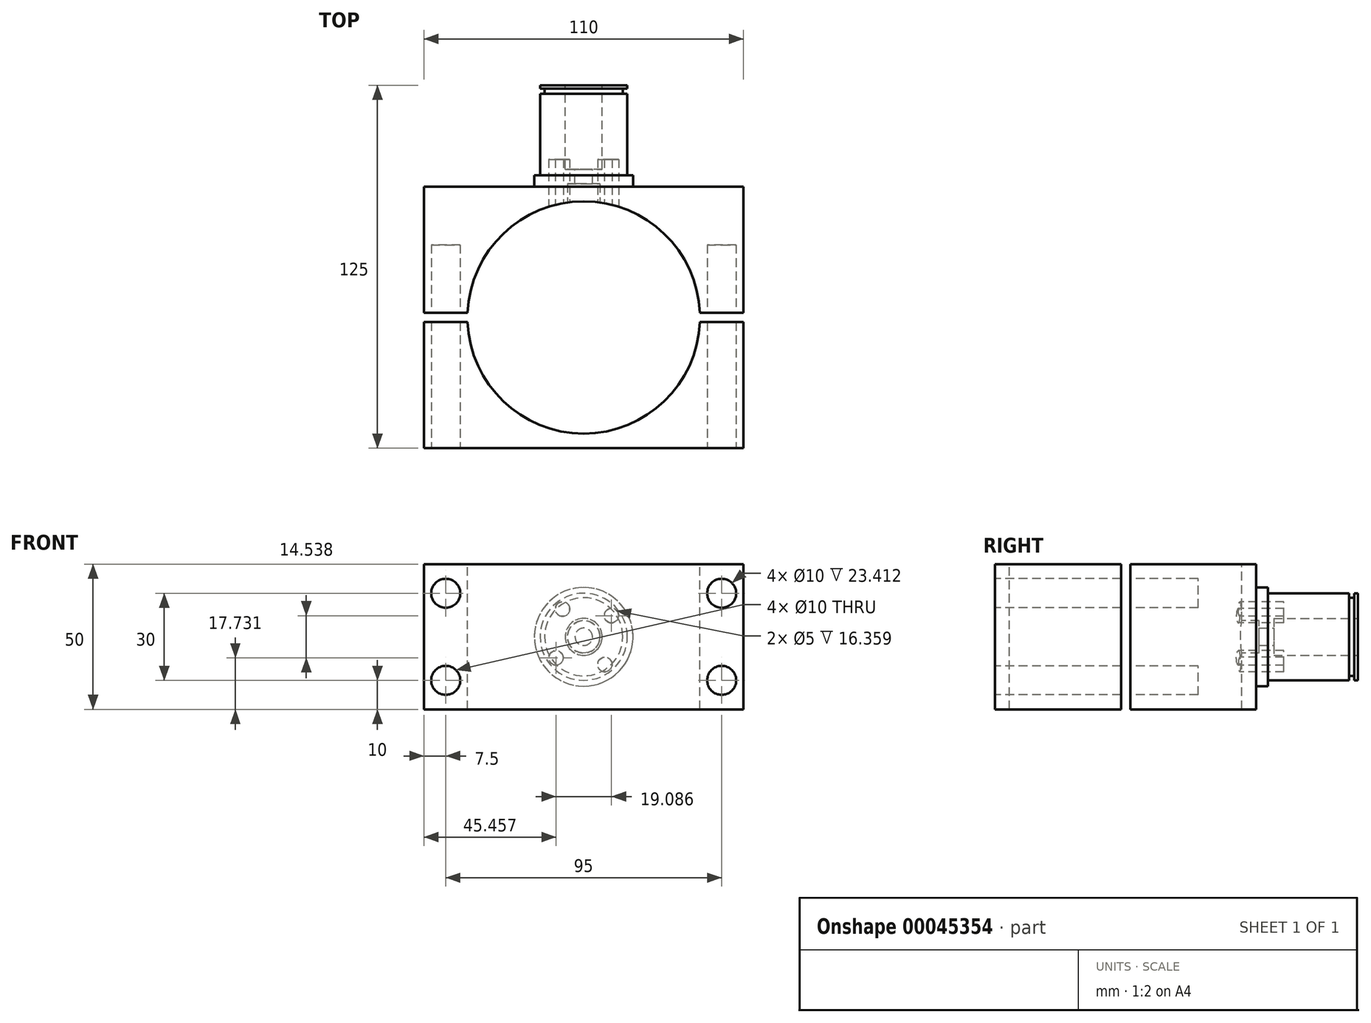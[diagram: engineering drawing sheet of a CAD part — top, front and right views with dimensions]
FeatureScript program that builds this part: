
annotation { "Feature Type Name" : "Feature", "Feature Type Description" : "" }
export const myFeature = defineFeature(function(context is Context, id is Id, definition is map)
    precondition{}
    {
        {
            var Q0;
            Q0=qCreatedBy(makeId("Front.planeOp"),FACE);
            var sketch = newSketch(context, id + "F0", { "sketchPlane" : qUnion([Q0])});
            skCircle(sketch, "E0", {"center": v(0, 0) * mm, "radius": 15 * mm});
            skCircle(sketch, "E1", {"center": v(0, 0) * mm, "radius": 6.36 * mm});
            skSolve(sketch);
        }
        {
            var Q0;
            Q0 = qSketchRegion(id + "F0", true);
            extrude(context, id + "F1", {"entities" : qUnion([Q0]), "depth" : 35 * mm});
        }
        {
            var Q0;
            Q0=makeQuery(id+"F1.opExtrude","CAP_FACE",FACE,{"disambiguationData":[OSD([sQuery(id+"F0.wireOp",EDGE,"E0"),sQuery(id+"F0.wireOp",EDGE,"E1")])],"isStart":false});
            var sketch = newSketch(context, id + "F2", { "sketchPlane" : qUnion([Q0])});
            skLineSegment(sketch, "E2.bottom", {"start": v(-55, 25) * mm, "end": v(55, 25) * mm});
            skLineSegment(sketch, "E2.top", {"start": v(-55, -25) * mm, "end": v(55, -25) * mm});
            skLineSegment(sketch, "E2.left", {"start": v(-55, 25) * mm, "end": v(-55, -25) * mm});
            skLineSegment(sketch, "E2.right", {"start": v(55, 25) * mm, "end": v(55, -25) * mm});
            skSolve(sketch);
        }
        {
            var Q0;
            Q0 = qSketchRegion(id + "F2", true);
            extrude(context, id + "F3", {"entities" : qUnion([Q0]), "operationType" : NewBodyOperationType.ADD, "depth" : 90 * mm});
        }
        {
            var Q0;
            Q0=makeQuery(id+"F3.opExtrude","CAP_FACE",FACE,{"disambiguationData":[OSD([sQuery(id+"F2.wireOp",EDGE,"E2.bottom"),sQuery(id+"F2.wireOp",EDGE,"E2.top"),sQuery(id+"F2.wireOp",EDGE,"E2.left"),sQuery(id+"F2.wireOp",EDGE,"E2.right")])],"isStart":false});
            var sketch = newSketch(context, id + "F4", { "sketchPlane" : qUnion([Q0])});
            skCircle(sketch, "E3", {"center": v(-47.5, 15) * mm, "radius": 5 * mm});
            skCircle(sketch, "E4.0.1.0", {"center": v(-47.5, -15) * mm, "radius": 5 * mm});
            skCircle(sketch, "E4.1.0.0", {"center": v(47.5, 15) * mm, "radius": 5 * mm});
            skCircle(sketch, "E4.1.1.0", {"center": v(47.5, -15) * mm, "radius": 5 * mm});
            skLineSegment(sketch, "E4.direction1", {"start": v(-47.5, 15) * mm, "end": v(47.5, 15) * mm, "construction": true});
            skLineSegment(sketch, "E4.direction2", {"start": v(-47.5, 15) * mm, "end": v(-47.5, -15) * mm, "construction": true});
            skSolve(sketch);
        }
        {
            var Q0;
            Q0 = qSketchRegion(id + "F4", true);
            var Q1;
            Q1=makeQuery(id+"F7.boolean.opBoolean","COPY",FACE,{"derivedFrom":makeQuery(id+"F7.opExtrude","SWEPT_FACE",FACE,{"disambiguationData":[OSD([sQuery(id+"F6.wireOp",EDGE,"E6.bottom")])]})});
            var Q2;
            Q2=makeQuery(id+"F7.boolean.opBoolean","COPY",FACE,{"derivedFrom":makeQuery(id+"F7.opExtrude","SWEPT_FACE",FACE,{"disambiguationData":[OSD([sQuery(id+"F6.wireOp",EDGE,"E7.trimOffspring")])]})});
            extrude(context, id + "F5", {"entities" : qUnion([Q0, Q1, Q2]), "operationType" : NewBodyOperationType.REMOVE, "oppositeDirection" : true, "depth" : 70 * mm});
        }
        {
            var Q0;
            Q0=makeQuery(id+"F3.opExtrude","SWEPT_FACE",FACE,{"disambiguationData":[OSD([sQuery(id+"F2.wireOp",EDGE,"E2.bottom")])]});
            var sketch = newSketch(context, id + "F6", { "sketchPlane" : qUnion([Q0])});
            skArc(sketch, "E5", {"start": v(-39.97, -81.59) * mm, "mid": v(0, -120) * mm, "end": v(39.97, -81.59) * mm});
            skLineSegment(sketch, "E6.bottom", {"start": v(-59, -78.41) * mm, "end": v(-39.97, -78.41) * mm});
            skLineSegment(sketch, "E6.top", {"start": v(-59, -81.59) * mm, "end": v(-39.97, -81.59) * mm});
            skLineSegment(sketch, "E6.left", {"start": v(-59, -78.41) * mm, "end": v(-59, -81.59) * mm});
            skLineSegment(sketch, "E6.right", {"start": v(59.74, -78.41) * mm, "end": v(59.74, -81.59) * mm});
            skLineSegment(sketch, "E7.trimOffspring", {"start": v(39.97, -78.41) * mm, "end": v(59.74, -78.41) * mm});
            skLineSegment(sketch, "E8.trimOffspring", {"start": v(39.97, -81.59) * mm, "end": v(59.74, -81.59) * mm});
            skArc(sketch, "E9.trimOffspring", {"start": v(39.97, -78.41) * mm, "mid": v(0, -40) * mm, "end": v(-39.97, -78.41) * mm});
            skSolve(sketch);
        }
        {
            var Q0;
            Q0 = qSketchRegion(id + "F6", true);
            extrude(context, id + "F7", {"entities" : qUnion([Q0]), "operationType" : NewBodyOperationType.REMOVE, "endBound" : BoundingType.THROUGH_ALL, "oppositeDirection" : true, "depth" : 25 * mm});
        }
        {
            var Q0;
            Q0=makeQuery(id+"F1.opExtrude","CAP_FACE",FACE,{"disambiguationData":[OSD([sQuery(id+"F0.wireOp",EDGE,"E0"),sQuery(id+"F0.wireOp",EDGE,"E1")])],"isStart":true});
            var sketch = newSketch(context, id + "F8", { "sketchPlane" : qUnion([Q0])});
            skCircle(sketch, "E10", {"center": v(0, 0) * mm, "radius": 13.45 * mm});
            skCircle(sketch, "E11", {"center": v(0, 0) * mm, "radius": 15 * mm});
            skSolve(sketch);
        }
        {
            var Q0;
            Q0 = qSketchRegion(id + "F8", true);
            extrude(context, id + "F9", {"entities" : qUnion([Q0]), "operationType" : NewBodyOperationType.REMOVE, "oppositeDirection" : true, "depth" : 3 * mm});
        }
        {
            var Q0;
            Q0=makeQuery(id+"F1.opExtrude","CAP_FACE",FACE,{"disambiguationData":[OSD([sQuery(id+"F0.wireOp",EDGE,"E0"),sQuery(id+"F0.wireOp",EDGE,"E1")])],"isStart":true});
            var sketch = newSketch(context, id + "F10", { "sketchPlane" : qUnion([Q0])});
            skCircle(sketch, "E12", {"center": v(0, 0) * mm, "radius": 15 * mm});
            skCircle(sketch, "E13", {"center": v(0, 0) * mm, "radius": 13.45 * mm});
            skSolve(sketch);
        }
        {
            var Q0;
            Q0 = qSketchRegion(id + "F10", true);
            extrude(context, id + "F11", {"entities" : qUnion([Q0]), "operationType" : NewBodyOperationType.ADD, "oppositeDirection" : true, "depth" : 1.22 * mm});
        }
        {
            var Q0;
            {var subQ0=sQuery(id+"F2.wireOp",EDGE,"E2.left");var subQ1=sQuery(id+"F2.wireOp",EDGE,"E2.bottom");var subQ2=sQuery(id+"F2.wireOp",EDGE,"E2.top");var subQ3=sQuery(id+"F2.wireOp",EDGE,"E2.right");Q0=makeQuery(id+"F3.boolean.opBoolean","SPLIT",FACE,{"disambiguationData":[TD([makeQuery(id+"F1.opExtrude","SWEPT_FACE",FACE,{"disambiguationData":[OSD([sQuery(id+"F0.wireOp",EDGE,"E0")])]})])],"derivedFrom":makeQuery(id+"F3.opExtrude","CAP_FACE",FACE,{"disambiguationData":[OSD([subQ1,subQ2,subQ0,subQ3])],"isStart":true})});}
            var sketch = newSketch(context, id + "F12", { "sketchPlane" : qUnion([Q0])});
            skCircle(sketch, "E14", {"center": v(0, 0) * mm, "radius": 17 * mm});
            skSolve(sketch);
        }
        {
            var Q0;
            Q0=makeQuery(id+"F12.imprint","IMPRINT",FACE,{"disambiguationData":[TD([[makeQuery(id+"F12.imprint","IMPRINT",EDGE,{"derivedFrom":sQuery(id+"F12.wireOp",EDGE,"E14")}),1.0]])]});
            extrude(context, id + "F13", {"entities" : qUnion([Q0]), "operationType" : NewBodyOperationType.ADD, "depth" : 4 * mm});
        }
        {
            var Q0;
            Q0=makeQuery(id+"F3.boolean.opBoolean","SPLIT",FACE,{"disambiguationData":[TD([makeQuery(id+"F1.opExtrude","SWEPT_FACE",FACE,{"disambiguationData":[OSD([sQuery(id+"F0.wireOp",EDGE,"E1")])]})])],"derivedFrom":makeQuery(id+"F3.opExtrude","CAP_FACE",FACE,{"disambiguationData":[OSD([sQuery(id+"F2.wireOp",EDGE,"E2.bottom"),sQuery(id+"F2.wireOp",EDGE,"E2.top"),sQuery(id+"F2.wireOp",EDGE,"E2.left"),sQuery(id+"F2.wireOp",EDGE,"E2.right")])],"isStart":true})});
            var sketch = newSketch(context, id + "F14", { "sketchPlane" : qUnion([Q0])});
            skCircle(sketch, "E15", {"center": v(0, 0) * mm, "radius": 7.83 * mm});
            skSolve(sketch);
        }
        {
            var Q0;
            Q0 = qSketchRegion(id + "F14", true);
            extrude(context, id + "F15", {"entities" : qUnion([Q0]), "operationType" : NewBodyOperationType.ADD, "depth" : 6 * mm});
        }
        {
            var Q0;
            Q0=makeQuery(id+"F15.opExtrude","CAP_FACE",FACE,{"disambiguationData":[OSD([sQuery(id+"F14.wireOp",EDGE,"E15")])],"isStart":false});
            var sketch = newSketch(context, id + "F16", { "sketchPlane" : qUnion([Q0])});
            skCircle(sketch, "E16", {"center": v(0, 0) * mm, "radius": 3 * mm});
            skSolve(sketch);
        }
        {
            var Q0;
            Q0 = qSketchRegion(id + "F16", true);
            extrude(context, id + "F17", {"entities" : qUnion([Q0]), "operationType" : NewBodyOperationType.REMOVE, "oppositeDirection" : true, "depth" : 25 * mm});
        }
        {
            var Q0;
            Q0=qCreatedBy(makeId("Front.planeOp"),FACE);
            cPlane(context, id + "F18", {"entities" : qUnion([Q0]), "cplaneType" : CPlaneType.OFFSET, "offset" : 40.5 * mm, "width" : 150 * mm, "height" : 150 * mm});
        }
        {
            var Q0;
            Q0=qCreatedBy(id+"F18.planeOp",FACE);
            var sketch = newSketch(context, id + "F19", { "sketchPlane" : qUnion([Q0])});
            skCircle(sketch, "E17", {"center": v(0, 0) * mm, "radius": 5.6 * mm});
            skCircle(sketch, "E18", {"center": v(-7.27, 9.54) * mm, "radius": 2.5 * mm});
            skCircle(sketch, "E19.1.0", {"center": v(-9.54, -7.27) * mm, "radius": 2.5 * mm});
            skCircle(sketch, "E19.2.0", {"center": v(7.27, -9.54) * mm, "radius": 2.5 * mm});
            skCircle(sketch, "E19.3.0", {"center": v(9.54, 7.27) * mm, "radius": 2.5 * mm});
            skSolve(sketch);
        }
        {
            var Q0;
            Q0=makeQuery(id+"F19.imprint","IMPRINT",FACE,{"disambiguationData":[TD([[makeQuery(id+"F19.imprint","IMPRINT",EDGE,{"derivedFrom":sQuery(id+"F19.wireOp",EDGE,"E17")}),1.0]])]});
            extrude(context, id + "F20", {"entities" : qUnion([Q0]), "operationType" : NewBodyOperationType.REMOVE, "oppositeDirection" : true, "depth" : 6.5 * mm});
        }
        {
            var Q0;
            Q0=makeQuery(id+"F19.imprint","IMPRINT",FACE,{"disambiguationData":[TD([[makeQuery(id+"F19.imprint","IMPRINT",EDGE,{"derivedFrom":sQuery(id+"F19.wireOp",EDGE,"E19.2.0")}),1.0]])]});
            var Q1;
            Q1=makeQuery(id+"F19.imprint","IMPRINT",FACE,{"disambiguationData":[TD([[makeQuery(id+"F19.imprint","IMPRINT",EDGE,{"derivedFrom":sQuery(id+"F19.wireOp",EDGE,"E19.3.0")}),1.0]])]});
            var Q2;
            Q2=makeQuery(id+"F19.imprint","IMPRINT",FACE,{"disambiguationData":[TD([[makeQuery(id+"F19.imprint","IMPRINT",EDGE,{"derivedFrom":sQuery(id+"F19.wireOp",EDGE,"E18")}),1.0]])]});
            var Q3;
            Q3=makeQuery(id+"F19.imprint","IMPRINT",FACE,{"disambiguationData":[TD([[makeQuery(id+"F19.imprint","IMPRINT",EDGE,{"derivedFrom":sQuery(id+"F19.wireOp",EDGE,"E19.1.0")}),1.0]])]});
            extrude(context, id + "F21", {"entities" : qUnion([Q0, Q1, Q2, Q3]), "operationType" : NewBodyOperationType.REMOVE, "oppositeDirection" : true, "depth" : 15 * mm, "hasSecondDirection" : true, "secondDirectionOppositeDirection" : false, "secondDirectionDepth" : 25 * mm});
        }
    });
